annotation { "Feature Type Name" : "Feature", "Feature Type Description" : "" }
export const myFeature = defineFeature(function(context is Context, id is Id, definition is map)
    precondition{}
    {
        {
            var Q0;
            Q0=qCreatedBy(makeId("Top.planeOp"),FACE);
            var sketch = newSketch(context, id + "F0", { "sketchPlane" : qUnion([Q0])});
            skLineSegment(sketch, "E0.bottom", {"start": v(50, -20) * mm, "end": v(-50, -20) * mm});
            skLineSegment(sketch, "E0.top", {"start": v(50, 20) * mm, "end": v(-50, 20) * mm});
            skLineSegment(sketch, "E0.left", {"start": v(50, -20) * mm, "end": v(50, 20) * mm});
            skLineSegment(sketch, "E0.right", {"start": v(-50, -20) * mm, "end": v(-50, 20) * mm});
            skPoint(sketch, "E0.middle", {"position": v(0, 0) * mm});
            skLineSegment(sketch, "E1", {"start": v(0, 0) * mm, "end": v(50, 0) * mm, "construction": true});
            skLineSegment(sketch, "E2", {"start": v(25, 0) * mm, "end": v(25, 20) * mm, "construction": true});
            skLineSegment(sketch, "E3", {"start": v(25, 10) * mm, "end": v(50, 10) * mm, "construction": true});
            skLineSegment(sketch, "E4", {"start": v(25, 10) * mm, "end": v(0, 10) * mm, "construction": true});
            skLineSegment(sketch, "E5", {"start": v(25, 0) * mm, "end": v(25, -20) * mm, "construction": true});
            skLineSegment(sketch, "E6", {"start": v(25, -10) * mm, "end": v(50, -10) * mm, "construction": true});
            skLineSegment(sketch, "E7", {"start": v(25, -10) * mm, "end": v(0, -10) * mm, "construction": true});
            skLineSegment(sketch, "E8", {"start": v(12.5, 10) * mm, "end": v(12.5, 0) * mm, "construction": true});
            skLineSegment(sketch, "E9", {"start": v(37.5, 10) * mm, "end": v(37.5, 0) * mm, "construction": true});
            skLineSegment(sketch, "E10", {"start": v(37.5, 0) * mm, "end": v(37.5, -10) * mm, "construction": true});
            skLineSegment(sketch, "E11", {"start": v(37.5, -10) * mm, "end": v(37.5, -20) * mm, "construction": true});
            skLineSegment(sketch, "E12", {"start": v(12.5, 0) * mm, "end": v(12.5, -10) * mm, "construction": true});
            skLineSegment(sketch, "E13", {"start": v(12.5, -10) * mm, "end": v(12.5, -20) * mm, "construction": true});
            skLineSegment(sketch, "E14", {"start": v(25, 20) * mm, "end": v(25, 10) * mm, "construction": true});
            skCircle(sketch, "E15", {"center": v(25, 15) * mm, "radius": 1.5 * mm});
            skLineSegment(sketch, "E16", {"start": v(25, 0) * mm, "end": v(25, -10) * mm, "construction": true});
            skCircle(sketch, "E17", {"center": v(25, -5) * mm, "radius": 1.5 * mm});
            skCircle(sketch, "E18", {"center": v(12.5, -15) * mm, "radius": 1.5 * mm});
            skCircle(sketch, "E19", {"center": v(37.5, -15) * mm, "radius": 1.5 * mm});
            skCircle(sketch, "E20", {"center": v(12.5, 5) * mm, "radius": 1.5 * mm});
            skCircle(sketch, "E21", {"center": v(37.5, 5) * mm, "radius": 1.5 * mm});
            skLineSegment(sketch, "E22", {"start": v(0, 0) * mm, "end": v(-50, 0) * mm, "construction": true});
            skCircle(sketch, "E23", {"center": v(-25, 0) * mm, "radius": 3 * mm});
            skLineSegment(sketch, "E24.bottom", {"start": v(48, -18) * mm, "end": v(-48, -18) * mm});
            skLineSegment(sketch, "E24.top", {"start": v(48, 18) * mm, "end": v(-48, 18) * mm});
            skLineSegment(sketch, "E24.left", {"start": v(48, -18) * mm, "end": v(48, 18) * mm});
            skLineSegment(sketch, "E24.right", {"start": v(-48, -18) * mm, "end": v(-48, 18) * mm});
            skLineSegment(sketch, "E25", {"start": v(-48, 18) * mm, "end": v(-48, 20) * mm, "construction": true});
            skLineSegment(sketch, "E26", {"start": v(-48, 18) * mm, "end": v(-50, 18) * mm, "construction": true});
            skLineSegment(sketch, "E27", {"start": v(48, -18) * mm, "end": v(50, -18) * mm, "construction": true});
            skLineSegment(sketch, "E28", {"start": v(48, -18) * mm, "end": v(48, -20) * mm, "construction": true});
            skSolve(sketch);
        }
        {
            var Q0;
            Q0=makeQuery(id+"F0.imprint","IMPRINT",FACE,{"disambiguationData":[TD([[makeQuery(id+"F0.imprint","IMPRINT",EDGE,{"derivedFrom":sQuery(id+"F0.wireOp",EDGE,"E15")}),-1.0]])]});
            extrude(context, id + "F1", {"entities" : qUnion([Q0]), "oppositeDirection" : true, "depth" : 2 * mm, "offsetDistance" : 25 * mm});
        }
        {
            var Q0;
            Q0 = qSketchRegion(id + "F0", true);
            extrude(context, id + "F2", {"entities" : qUnion([Q0]), "operationType" : NewBodyOperationType.ADD, "oppositeDirection" : true, "depth" : 4 * mm, "offsetDistance" : 25 * mm});
        }
        {
            var Q0;
            {var subQ0=sQuery(id+"F0.wireOp",EDGE,"E24.right");var subQ1=sQuery(id+"F0.wireOp",EDGE,"E24.left");var subQ2=sQuery(id+"F0.wireOp",EDGE,"E24.top");var subQ3=sQuery(id+"F0.wireOp",EDGE,"E24.bottom");Q0=makeQuery(id+"F2.boolean.opBoolean","MERGE",FACE,{"derivedFrom":[makeQuery(id+"F1.opExtrude","CAP_FACE",FACE,{"disambiguationData":[OSD([sQuery(id+"F0.wireOp",EDGE,"E15"),sQuery(id+"F0.wireOp",EDGE,"E17"),sQuery(id+"F0.wireOp",EDGE,"E18"),sQuery(id+"F0.wireOp",EDGE,"E19"),sQuery(id+"F0.wireOp",EDGE,"E20"),sQuery(id+"F0.wireOp",EDGE,"E21"),sQuery(id+"F0.wireOp",EDGE,"E23"),subQ3,subQ2,subQ1,subQ0])],"isStart":true}),makeQuery(id+"F2.opExtrude","CAP_FACE",FACE,{"disambiguationData":[OSD([sQuery(id+"F0.wireOp",EDGE,"E0.bottom"),sQuery(id+"F0.wireOp",EDGE,"E0.top"),sQuery(id+"F0.wireOp",EDGE,"E0.left"),sQuery(id+"F0.wireOp",EDGE,"E0.right"),subQ3,subQ2,subQ1,subQ0])],"isStart":true})]});}
            var sketch = newSketch(context, id + "F3", { "sketchPlane" : qUnion([Q0])});
            skText(sketch, "E29", { "text": "Landing Gear", "fontName": "OpenSans-Regular.ttf"});
            skText(sketch, "E30", { "text": "UP", "fontName": "OpenSans-Regular.ttf"});
            skText(sketch, "E31", { "text": "Down", "fontName": "OpenSans-Regular.ttf"});
            const initialGuessF3  = {"E29": [-0.04727, 0.0099, 1, 0, 0.00542], "E30": [-0.01754, 0.00193, 1, 0, 0.00583], "E31": [-0.02649, -0.01168, 1, 0, 0.00664]};
            skSetInitialGuess(sketch, initialGuessF3);
            skSolve(sketch);
        }
        {
            var Q0;
            Q0 = qSketchRegion(id + "F3", true);
            extrude(context, id + "F4", {"entities" : qUnion([Q0]), "operationType" : NewBodyOperationType.REMOVE, "oppositeDirection" : true, "depth" : 1 * mm, "offsetDistance" : 25 * mm});
        }
    });